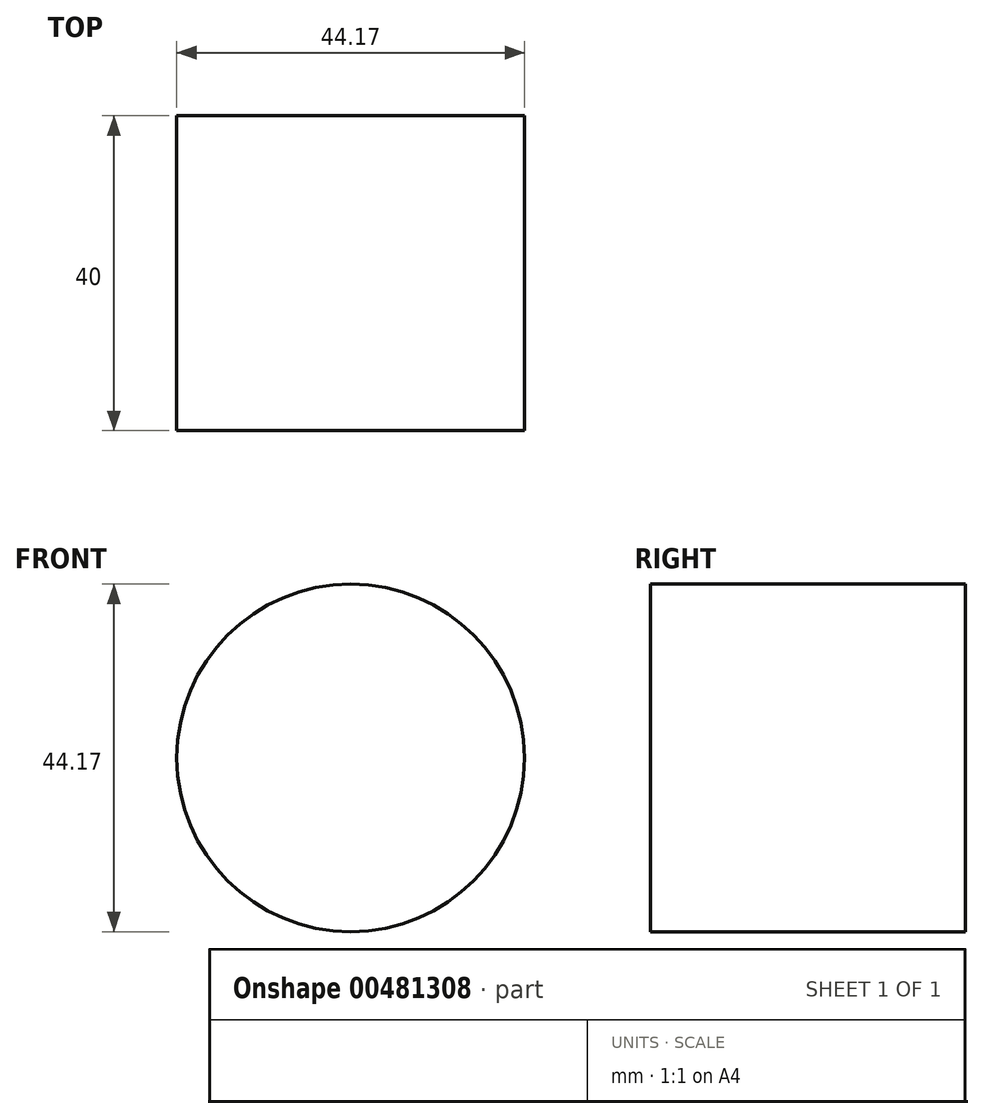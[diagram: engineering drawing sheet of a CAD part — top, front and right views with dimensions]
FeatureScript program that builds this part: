
annotation { "Feature Type Name" : "Feature", "Feature Type Description" : "" }
export const myFeature = defineFeature(function(context is Context, id is Id, definition is map)
    precondition{}
    {
        {
            var Q0;
            Q0=qCreatedBy(makeId("Front.planeOp"),FACE);
            var sketch = newSketch(context, id + "F0", { "sketchPlane" : qUnion([Q0])});
            skCircle(sketch, "E0", {"center": v(25.01, 38.61) * mm, "radius": 22.08 * mm});
            skSolve(sketch);
        }
        {
            var Q0;
            Q0=makeQuery(id+"F0.imprint","IMPRINT",FACE,{"disambiguationData":[TD([[makeQuery(id+"F0.imprint","IMPRINT",EDGE,{"derivedFrom":sQuery(id+"F0.wireOp",EDGE,"E0")}),1.0]])]});
            extrude(context, id + "F1", {"entities" : qUnion([Q0]), "depth" : 40 * mm});
        }
    });
